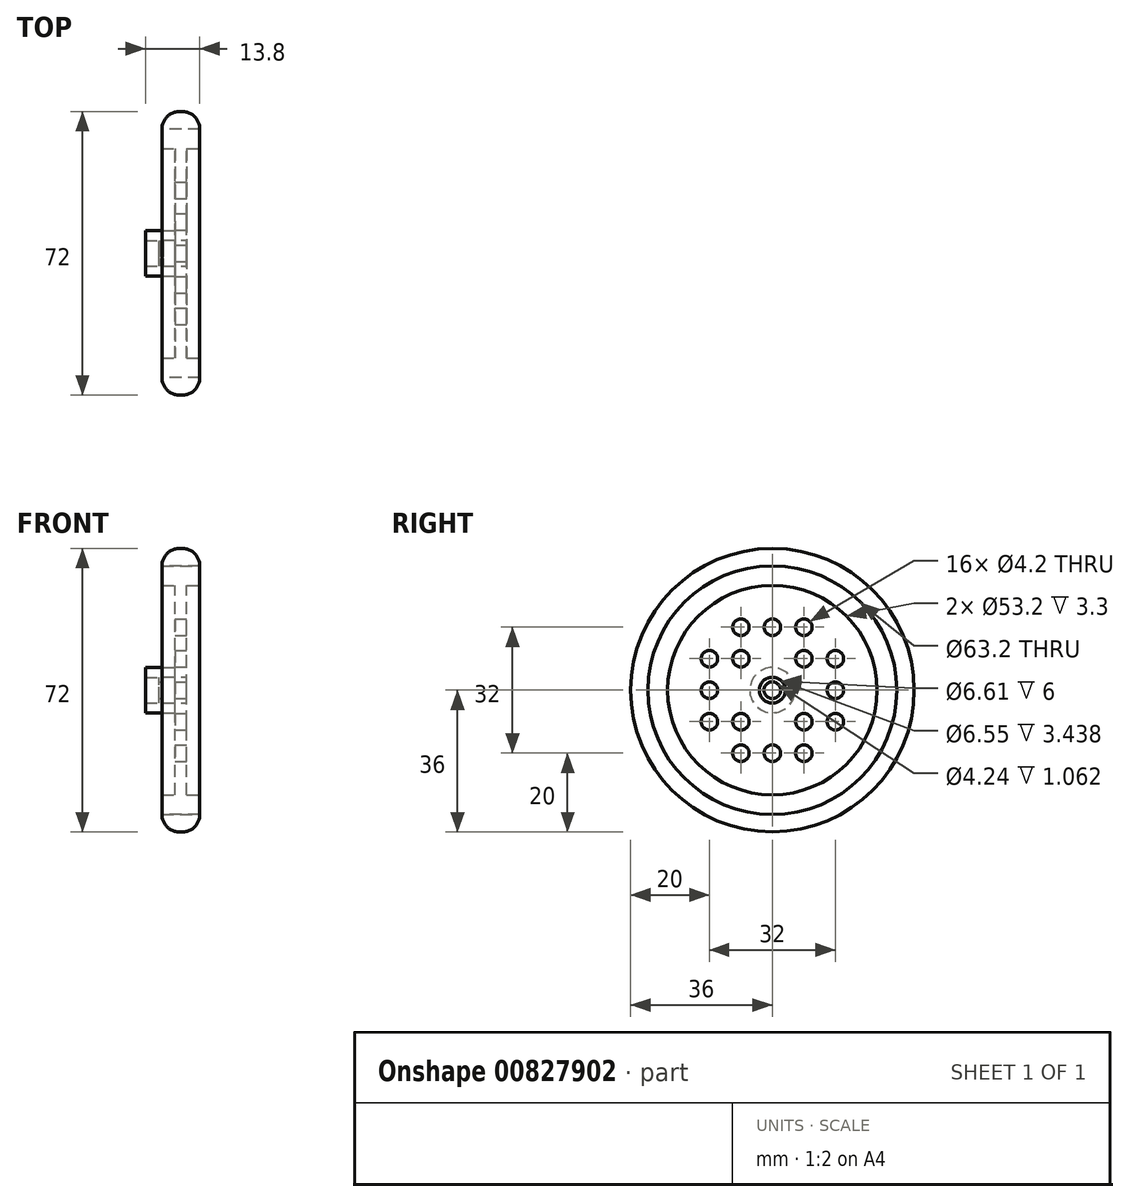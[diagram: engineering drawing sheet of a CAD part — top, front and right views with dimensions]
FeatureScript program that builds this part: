
annotation { "Feature Type Name" : "Feature", "Feature Type Description" : "" }
export const myFeature = defineFeature(function(context is Context, id is Id, definition is map)
    precondition{}
    {
        {
            var Q0;
            Q0=qCreatedBy(makeId("Front.planeOp"),FACE);
            var sketch = newSketch(context, id + "F0", { "sketchPlane" : qUnion([Q0])});
            skLineSegment(sketch, "E0", {"start": v(-3.3, 3.3) * mm, "end": v(-3.3, 26.6) * mm});
            skLineSegment(sketch, "E1", {"start": v(-3.3, 26.6) * mm, "end": v(0, 26.6) * mm});
            skLineSegment(sketch, "E2", {"start": v(0, 26.6) * mm, "end": v(0, 31.6) * mm});
            skLineSegment(sketch, "E3", {"start": v(0, 31.6) * mm, "end": v(-9.6, 31.6) * mm});
            skLineSegment(sketch, "E4", {"start": v(-9.6, 31.6) * mm, "end": v(-9.6, 26.6) * mm});
            skLineSegment(sketch, "E5", {"start": v(-9.6, 26.6) * mm, "end": v(-6.3, 26.6) * mm});
            skLineSegment(sketch, "E6", {"start": v(-6.3, 26.6) * mm, "end": v(-6.3, 5.75) * mm});
            skLineSegment(sketch, "E7", {"start": v(-6.3, 5.75) * mm, "end": v(-13.8, 5.75) * mm});
            skLineSegment(sketch, "E8", {"start": v(-3.3, 3.3) * mm, "end": v(-9.3, 3.3) * mm});
            skLineSegment(sketch, "E9", {"start": v(-9.3, 3.3) * mm, "end": v(-9.3, 2.12) * mm});
            skLineSegment(sketch, "E10", {"start": v(-9.3, 2.12) * mm, "end": v(-10.36, 2.12) * mm});
            skLineSegment(sketch, "E11", {"start": v(-10.36, 2.12) * mm, "end": v(-10.36, 3.28) * mm});
            skLineSegment(sketch, "E12", {"start": v(-10.36, 3.28) * mm, "end": v(-13.8, 3.28) * mm});
            skLineSegment(sketch, "E13", {"start": v(-13.8, 3.28) * mm, "end": v(-13.8, 5.75) * mm});
            skPoint(sketch, "E14.orphan", {"position": v(-15.5, 3.28) * mm});
            skLineSegment(sketch, "E15", {"start": v(8.19, 0) * mm, "end": v(0, 0) * mm, "construction": true});
            skPoint(sketch, "E16.orphan", {"position": v(-6.3, 0) * mm});
            skPoint(sketch, "E17.orphan", {"position": v(-3.3, 0) * mm});
            skSolve(sketch);
        }
        {
            var Q0;
            Q0=makeQuery(id+"F0.imprint","IMPRINT",FACE,{"disambiguationData":[TD([[makeQuery(id+"F0.imprint","IMPRINT",EDGE,{"derivedFrom":sQuery(id+"F0.wireOp",EDGE,"E0")}),1.0]])]});
            var Q1;
            Q1=sQuery(id+"F0.wireOp",EDGE,"E15");
            revolve(context, id + "F1", {"surfaceOperationType" : NewSurfaceOperationType.NEW, "entities" : qUnion([Q0]), "axis" : qUnion([Q1]), "revolveType" : RevolveType.FULL});
        }
        {
            var Q0;
            Q0=makeQuery(id+"F1.opRevolve","SWEPT_FACE",FACE,{"disambiguationData":[OSD([sQuery(id+"F0.wireOp",EDGE,"E0")])]});
            var sketch = newSketch(context, id + "F2", { "sketchPlane" : qUnion([Q0])});
            skLineSegment(sketch, "E18.bottom", {"start": v(16, 16) * mm, "end": v(-16, 16) * mm, "construction": true});
            skLineSegment(sketch, "E18.top", {"start": v(16, -16) * mm, "end": v(-16, -16) * mm, "construction": true});
            skLineSegment(sketch, "E18.left", {"start": v(16, 16) * mm, "end": v(16, -16) * mm, "construction": true});
            skLineSegment(sketch, "E18.right", {"start": v(-16, 16) * mm, "end": v(-16, -16) * mm, "construction": true});
            skPoint(sketch, "E18.middle", {"position": v(0, 0) * mm});
            skLineSegment(sketch, "E19.bottom", {"start": v(8, 8) * mm, "end": v(-8, 8) * mm, "construction": true});
            skLineSegment(sketch, "E19.top", {"start": v(8, -8) * mm, "end": v(-8, -8) * mm, "construction": true});
            skLineSegment(sketch, "E19.left", {"start": v(8, 8) * mm, "end": v(8, -8) * mm, "construction": true});
            skLineSegment(sketch, "E19.right", {"start": v(-8, 8) * mm, "end": v(-8, -8) * mm, "construction": true});
            skCircle(sketch, "E20", {"center": v(0, 16) * mm, "radius": 2.1 * mm});
            skCircle(sketch, "E21", {"center": v(-8, 8) * mm, "radius": 2.1 * mm});
            skCircle(sketch, "E22", {"center": v(-16, 0) * mm, "radius": 2.1 * mm});
            skCircle(sketch, "E23", {"center": v(-8, -8) * mm, "radius": 2.1 * mm});
            skCircle(sketch, "E24", {"center": v(0, -16) * mm, "radius": 2.1 * mm});
            skCircle(sketch, "E25", {"center": v(8, -8) * mm, "radius": 2.1 * mm});
            skCircle(sketch, "E26", {"center": v(16, 0) * mm, "radius": 2.1 * mm});
            skCircle(sketch, "E27", {"center": v(8, 8) * mm, "radius": 2.1 * mm});
            skCircle(sketch, "E28", {"center": v(-16, 8) * mm, "radius": 2.1 * mm});
            skCircle(sketch, "E29", {"center": v(-8, 16) * mm, "radius": 2.1 * mm});
            skCircle(sketch, "E30", {"center": v(8, 16) * mm, "radius": 2.1 * mm});
            skCircle(sketch, "E31", {"center": v(16, 8) * mm, "radius": 2.1 * mm});
            skCircle(sketch, "E32", {"center": v(16, -8) * mm, "radius": 2.1 * mm});
            skCircle(sketch, "E33", {"center": v(-8, -16) * mm, "radius": 2.1 * mm});
            skCircle(sketch, "E34", {"center": v(8, -16) * mm, "radius": 2.1 * mm});
            skCircle(sketch, "E35", {"center": v(-16, -8) * mm, "radius": 2.1 * mm});
            skSolve(sketch);
        }
        {
            var Q0;
            Q0 = qSketchRegion(id + "F2", true);
            extrude(context, id + "F3", {"entities" : qUnion([Q0]), "operationType" : NewBodyOperationType.REMOVE, "oppositeDirection" : true, "depth" : 25 * mm, "offsetDistance" : 25 * mm});
        }
        {
            var Q0;
            Q0=qCreatedBy(makeId("Top.planeOp"),FACE);
            var sketch = newSketch(context, id + "F4", { "sketchPlane" : qUnion([Q0])});
            skLineSegment(sketch, "E36", {"start": v(0, -31.6) * mm, "end": v(-9.6, -31.6) * mm, "construction": true});
            skLineSegment(sketch, "E37.0", {"start": v(-9.6, 31.6) * mm, "end": v(-9.6, -31.6) * mm, "construction": true});
            skLineSegment(sketch, "E38", {"start": v(-4.4, -36) * mm, "end": v(-5.2, -36) * mm});
            skArc(sketch, "E39", {"start": v(-9.6, -31.6) * mm, "mid": v(-8.31, -34.71) * mm, "end": v(-5.2, -36) * mm});
            skArc(sketch, "E40", {"start": v(-4.4, -36) * mm, "mid": v(-1.29, -34.71) * mm, "end": v(0, -31.6) * mm});
            skLineSegment(sketch, "E41.0", {"start": v(0, 31.6) * mm, "end": v(0, -31.6) * mm, "construction": true});
            skPoint(sketch, "E42.orphan", {"position": v(0, -36) * mm});
            skLineSegment(sketch, "E43", {"start": v(-9.6, -31.6) * mm, "end": v(0, -31.6) * mm});
            skLineSegment(sketch, "E44", {"start": v(-16.38, 0) * mm, "end": v(18.2, 0) * mm, "construction": true});
            skSolve(sketch);
        }
        {
            var Q0;
            Q0 = qSketchRegion(id + "F4", true);
            var Q1;
            Q1=sQuery(id+"F4.wireOp",EDGE,"E44");
            revolve(context, id + "F5", {"surfaceOperationType" : NewSurfaceOperationType.NEW, "entities" : qUnion([Q0]), "axis" : qUnion([Q1]), "revolveType" : RevolveType.FULL});
        }
    });
